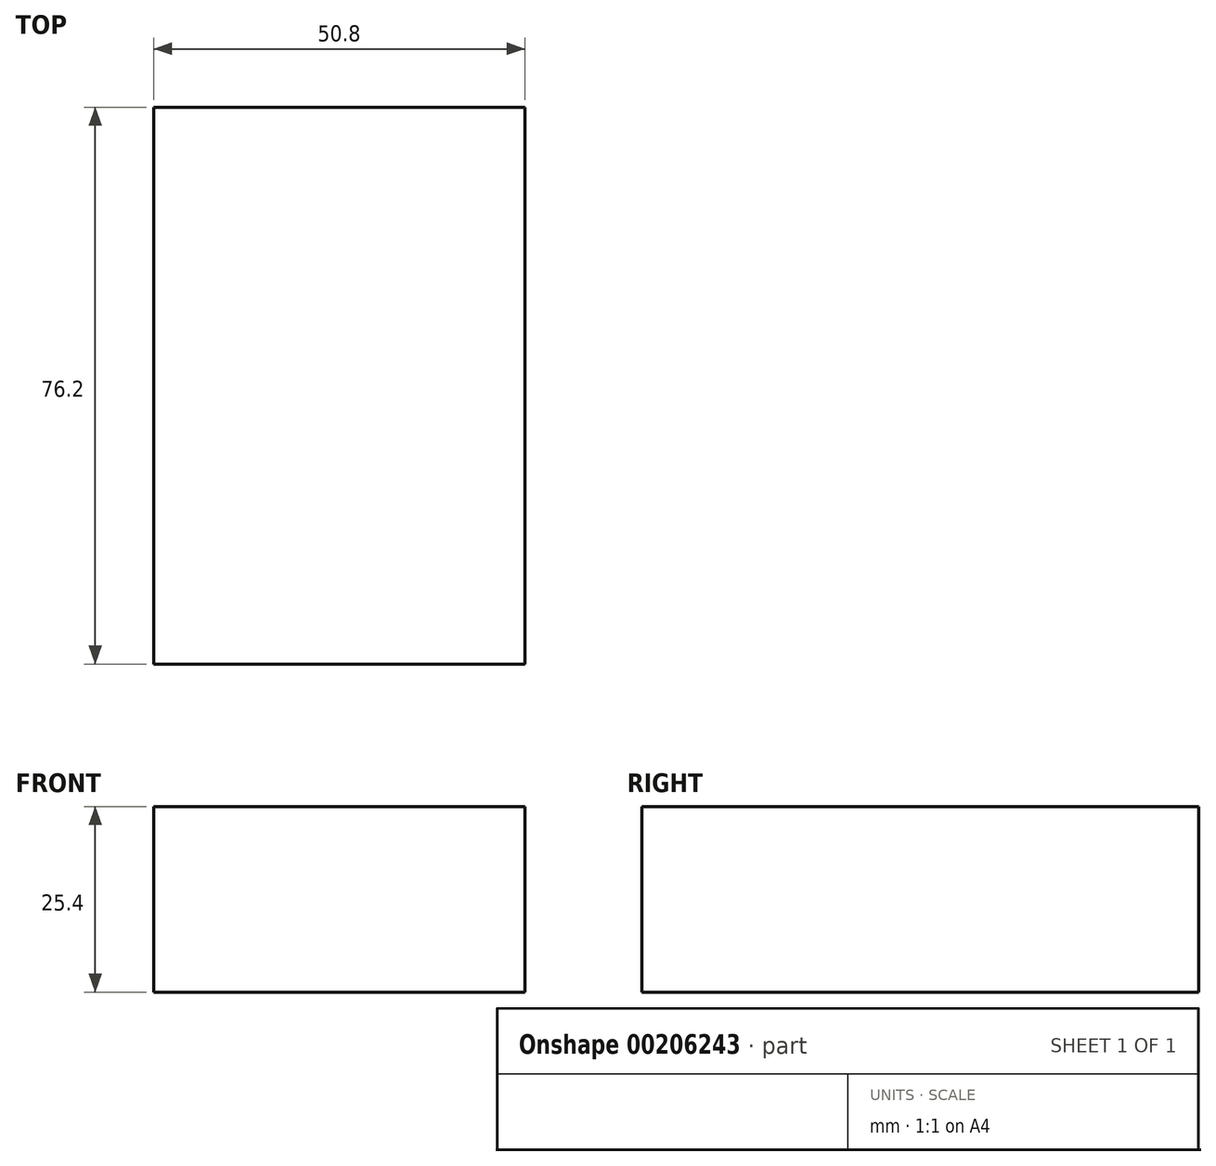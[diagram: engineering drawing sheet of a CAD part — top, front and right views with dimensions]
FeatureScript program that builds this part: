
annotation { "Feature Type Name" : "Feature", "Feature Type Description" : "" }
export const myFeature = defineFeature(function(context is Context, id is Id, definition is map)
    precondition{}
    {
        {
            var Q0;
            Q0=qCreatedBy(makeId("Right.planeOp"),FACE);
            var sketch = newSketch(context, id + "F0", { "sketchPlane" : qUnion([Q0])});
            skLineSegment(sketch, "E0.bottom", {"start": v(38.1, 12.7) * mm, "end": v(-38.1, 12.7) * mm});
            skLineSegment(sketch, "E0.top", {"start": v(38.1, -12.7) * mm, "end": v(-38.1, -12.7) * mm});
            skLineSegment(sketch, "E0.left", {"start": v(38.1, 12.7) * mm, "end": v(38.1, -12.7) * mm});
            skLineSegment(sketch, "E0.right", {"start": v(-38.1, 12.7) * mm, "end": v(-38.1, -12.7) * mm});
            skPoint(sketch, "E0.middle", {"position": v(0, 0) * mm});
            skSolve(sketch);
        }
        {
            var Q0;
            Q0 = qSketchRegion(id + "F0", true);
            extrude(context, id + "F1", {"entities" : qUnion([Q0]), "depth" : 50.8 * mm});
        }
    });
